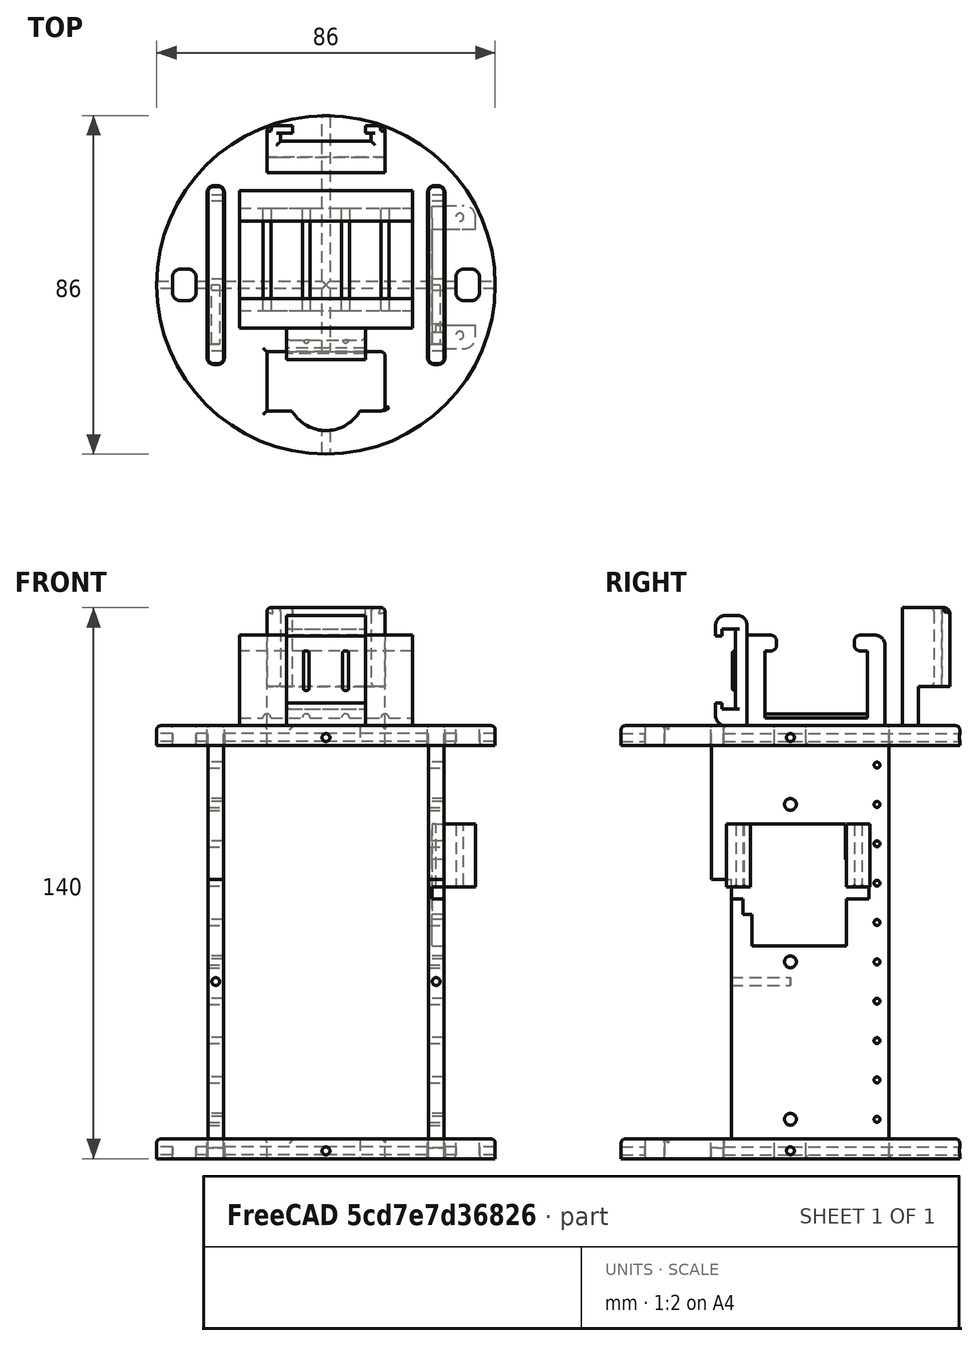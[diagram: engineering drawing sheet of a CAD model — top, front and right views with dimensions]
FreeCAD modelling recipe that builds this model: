
FCSTD DOCUMENT  (FreeCAD 1.0R39109 (Git))
Label: LateralDerecho_Capsula
License: All rights reserved
LicenseURL: http://en.wikipedia.org/wiki/All_rights_reserved
objects: Part::Cut×130, Part::Cylinder×98, Part::Fillet×96, Part::Box×72, Part::MultiFuse×37, Part::Offset×12, Part::Chamfer×1
note: 446 computed .brp shape members not serialized (recipe doc carries the construction recipe); baked Part::Feature solids carry a one-line shape summary decoded from their .brp

FEATURE [Part::Box] Box  label="Extensor"
  AttacherType = Attacher::AttachEngine3D
  Height = 66
  Length = 11
  Placement = pos=(30,-28,3) rot=(0,0,1;1.5708rad)
  Width = 60
FEATURE [Part::Box] Box001  label="Cubo001"
  AttacherType = Attacher::AttachEngine3D
  Height = 110
  Length = 45
  Placement = pos=(-30,25,0) rot=(0,0,-1;1.5708rad)
  Width = 4
FEATURE [Part::Box] Box002  label="Cubo002"
  AttacherType = Attacher::AttachEngine3D
  Height = 110
  Length = 45
  Placement = pos=(-30,25,0) rot=(0,0,-1;1.5708rad)
  Width = 4
FEATURE [Part::Box] Box003  label="Cubo003"
  AttacherType = Attacher::AttachEngine3D
  Height = 10
  Length = 30
  Placement = pos=(-15,-32,0) rot=(0,0,1;0rad)
  Width = 15
FEATURE [Part::Box] Box005  label="Cubo004"
  AttacherType = Attacher::AttachEngine3D
  Height = 15
  Length = 26
  Placement = pos=(-13,-23,110) rot=(0,0,1;0rad)
  Width = 35
FEATURE [Part::Box] Box006  label="Cubo005"
  AttacherType = Attacher::AttachEngine3D
  Height = 150
  Length = 6
  Width = 8
FEATURE [Part::Box] Box007  label="Cubo006"
  AttacherType = Attacher::AttachEngine3D
  Height = 150
  Length = 6
  Width = 8
FEATURE [Part::Box] Box008  label="Cubo007"
  AttacherType = Attacher::AttachEngine3D
  Height = 150
  Length = 6
  Width = 8
FEATURE [Part::Box] Box009  label="Cubo008"
  AttacherType = Attacher::AttachEngine3D
  Height = 150
  Length = 6
  Width = 8
FEATURE [Part::Box] Box010  label="Cubo009"
  AttacherType = Attacher::AttachEngine3D
  Height = 11.6
  Length = 20.8
  Placement = pos=(-10.5,-23,110) rot=(0,0,1;0rad)
  Width = 35
FEATURE [Part::Box] Box011  label="Cubo010"
  AttacherType = Attacher::AttachEngine3D
  Height = 11.6
  Length = 16
  Placement = pos=(-8,-23,116) rot=(0,0,1;0rad)
  Width = 35
FEATURE [Part::Box] Box095  label="Cubo095"
  AttacherType = Attacher::AttachEngine3D
  Height = 110
  Length = 45
  Placement = pos=(-30,25,0) rot=(0,0,-1;1.5708rad)
  Width = 4
FEATURE [Part::Box] Box096  label="Cubo096"
  AttacherType = Attacher::AttachEngine3D
  Height = 110
  Length = 45
  Placement = pos=(-30,25,0) rot=(0,0,-1;1.5708rad)
  Width = 4
FEATURE [Part::Box] Box097  label="Cubo097"
  AttacherType = Attacher::AttachEngine3D
  Height = 23
  Length = 24
  Width = 14
FEATURE [Part::Box] Box098  label="Cubo098"
  AttacherType = Attacher::AttachEngine3D
  Height = 3
  Length = 33.5
  Placement = pos=(-5,0,16) rot=(0,0,1;0rad)
  Width = 14
FEATURE [Part::Box] Box099  label="Cubo099"
  AttacherType = Attacher::AttachEngine3D
  Height = 1.4
  Length = 13
  Placement = pos=(9.8,5,28.6) rot=(0,0,1;0rad)
  Width = 4
FEATURE [Part::Box] Box100  label="Cubo100"
  AttacherType = Attacher::AttachEngine3D
  Height = 16
  Length = 10
  Placement = pos=(28,12.2,69) rot=(0,0,1;0rad)
  Width = 6
FEATURE [Part::Box] Box101  label="Cubo101"
  AttacherType = Attacher::AttachEngine3D
  Height = 16
  Length = 10
  Placement = pos=(28,-18.2,69) rot=(0,0,1;0rad)
  Width = 6
FEATURE [Part::Box] Box102  label="Extensor001"
  AttacherType = Attacher::AttachEngine3D
  Height = 66
  Length = 11
  Placement = pos=(30,-28,3) rot=(0,0,1;1.5708rad)
  Width = 60
FEATURE [Part::Box] Box104  label="Cubo102"
  AttacherType = Attacher::AttachEngine3D
  Height = 8
  Length = 20
  Width = 28
FEATURE [Part::Box] Box105  label="Cubo103"
  AttacherType = Attacher::AttachEngine3D
  Height = 2
  Length = 20.5
  Placement = pos=(0,4,4) rot=(0,0,1;0rad)
  Width = 20.5
FEATURE [Part::Box] Box106  label="Cubo104"
  AttacherType = Attacher::AttachEngine3D
  Height = 4
  Length = 20.5
  Placement = pos=(0,5,5) rot=(0,0,1;0rad)
  Width = 18.5
FEATURE [Part::Box] Box107  label="Cubo105"
  AttacherType = Attacher::AttachEngine3D
  Height = 8
  Length = 20
  Width = 30
FEATURE [Part::Box] Box108  label="Cubo106"
  AttacherType = Attacher::AttachEngine3D
  Height = 2
  Length = 20.5
  Placement = pos=(0,3.5,4) rot=(0,0,1;0rad)
  Width = 23
FEATURE [Part::Box] Box109  label="Cubo107"
  AttacherType = Attacher::AttachEngine3D
  Height = 4
  Length = 20.5
  Placement = pos=(0,5,5) rot=(0,0,1;0rad)
  Width = 18.5
FEATURE [Part::Box] Box110  label="Cubo108"
  AttacherType = Attacher::AttachEngine3D
  Height = 10
  Length = 20
  Placement = pos=(-9,-38,105) rot=(0,0,1;0rad)
  Width = 15
FEATURE [Part::Box] Box111  label="Cubo109"
  AttacherType = Attacher::AttachEngine3D
  Height = 110
  Length = 45
  Placement = pos=(-30,25,0) rot=(0,0,-1;1.5708rad)
  Width = 4
FEATURE [Part::Box] Box112  label="Extensor003"
  AttacherType = Attacher::AttachEngine3D
  Height = 66
  Length = 11
  Placement = pos=(30,-28,3) rot=(0,0,1;1.5708rad)
  Width = 60
FEATURE [Part::Box] Box113  label="Extensor004"
  AttacherType = Attacher::AttachEngine3D
  Height = 66
  Length = 11
  Placement = pos=(30,-28,3) rot=(0,0,1;1.5708rad)
  Width = 60
FEATURE [Part::Box] Box114  label="Cubo110"
  AttacherType = Attacher::AttachEngine3D
  Height = 110
  Length = 45
  Placement = pos=(-30,25,0) rot=(0,0,-1;1.5708rad)
  Width = 4
FEATURE [Part::Box] Box115  label="Cubo111"
  AttacherType = Attacher::AttachEngine3D
  Height = 23
  Length = 24
  Width = 14
FEATURE [Part::Box] Box116  label="Cubo112"
  AttacherType = Attacher::AttachEngine3D
  Height = 3
  Length = 33.5
  Placement = pos=(-5,0,16) rot=(0,0,1;0rad)
  Width = 14
FEATURE [Part::Box] Box117  label="Cubo113"
  AttacherType = Attacher::AttachEngine3D
  Height = 1.4
  Length = 13
  Placement = pos=(9.8,5,28.6) rot=(0,0,1;0rad)
  Width = 4
FEATURE [Part::Box] Box118  label="Cubo114"
  AttacherType = Attacher::AttachEngine3D
  Height = 16
  Length = 10
  Placement = pos=(28,12.2,69) rot=(0,0,1;0rad)
  Width = 6
FEATURE [Part::Box] Box119  label="Cubo115"
  AttacherType = Attacher::AttachEngine3D
  Height = 16
  Length = 10
  Placement = pos=(28,-18.2,69) rot=(0,0,1;0rad)
  Width = 6
FEATURE [Part::Box] Box120  label="Cubo116"
  AttacherType = Attacher::AttachEngine3D
  Height = 10
  Length = 4
  Placement = pos=(-30,-20,0) rot=(0,0,1;0rad)
  Width = 45
FEATURE [Part::Box] Box121  label="Cubo117"
  AttacherType = Attacher::AttachEngine3D
  Height = 10
  Length = 4
  Placement = pos=(-30,-20,0) rot=(0,0,1;0rad)
  Width = 45
FEATURE [Part::Box] Box122  label="Cubo118"
  AttacherType = Attacher::AttachEngine3D
  Height = 8
  Length = 20
  Width = 30
FEATURE [Part::Box] Box123  label="Cubo119"
  AttacherType = Attacher::AttachEngine3D
  Height = 2
  Length = 20.5
  Placement = pos=(0,3.5,4) rot=(0,0,1;0rad)
  Width = 23
FEATURE [Part::Box] Box124  label="Cubo120"
  AttacherType = Attacher::AttachEngine3D
  Height = 4
  Length = 20.5
  Placement = pos=(0,5,5) rot=(0,0,1;0rad)
  Width = 18.5
FEATURE [Part::Box] Box128  label="Cubo124"
  AttacherType = Attacher::AttachEngine3D
  Height = 30
  Length = 33
  Placement = pos=(-16,-43,115) rot=(0,0,1;0rad)
  Width = 30
FEATURE [Part::Box] Box129  label="Cubo125"
  AttacherType = Attacher::AttachEngine3D
  Height = 30
  Length = 33
  Placement = pos=(-16,13,110) rot=(0,0,1;0rad)
  Width = 30
FEATURE [Part::Box] Box130  label="Cubo126"
  AttacherType = Attacher::AttachEngine3D
  Height = 30
  Length = 30
  Placement = pos=(-16,13,110) rot=(0,0,1;0rad)
  Width = 4
FEATURE [Part::Box] Box131  label="Cubo127"
  AttacherType = Attacher::AttachEngine3D
  Height = 3.4
  Length = 21
  Placement = pos=(0,4.2,3) rot=(0,0,1;0rad)
  Width = 20.4
FEATURE [Part::Box] Box132  label="Cubo128"
  AttacherType = Attacher::AttachEngine3D
  Height = 4
  Length = 21
  Placement = pos=(0,5.75,6) rot=(0,0,1;0rad)
  Width = 17
FEATURE [Part::Box] Box133  label="Cubo129"
  AttacherType = Attacher::AttachEngine3D
  Height = 8
  Length = 20
  Width = 28
FEATURE [Part::Box] Box134  label="Cubo130"
  AttacherType = Attacher::AttachEngine3D
  Height = 16
  Length = 37
  Placement = pos=(-19,-15,110) rot=(0,0,1;0rad)
  Width = 30
FEATURE [Part::Box] Box135  label="Pila_ext"
  AttacherType = Attacher::AttachEngine3D
  Height = 25
  Length = 44
  Placement = pos=(-22,-11,110) rot=(0,0,1;0rad)
  Width = 35
FEATURE [Part::Box] Box136  label="Pila_int"
  AttacherType = Attacher::AttachEngine3D
  Height = 17
  Length = 44
  Placement = pos=(-22,-6.5,114) rot=(0,0,1;0rad)
  Width = 26
FEATURE [Part::Box] Box137  label="hueco_pila"
  AttacherType = Attacher::AttachEngine3D
  Height = 16.65
  Length = 44
  Placement = pos=(-22,-3.5,122) rot=(0,0,1;0rad)
  Width = 19.72
FEATURE [Part::Box] Box165  label="Cubo155"
  AttacherType = Attacher::AttachEngine3D
  Height = 17
  Length = 19
  Placement = pos=(27,-9.8,59) rot=(0,0,1;0rad)
  Width = 24
FEATURE [Part::Box] Box166  label="Cubo156"
  AttacherType = Attacher::AttachEngine3D
  Height = 66
  Length = 60
  Placement = pos=(-30,-20,5) rot=(0,0,1;0rad)
  Width = 5
FEATURE [Part::Box] Box167  label="Cubo157"
  AttacherType = Attacher::AttachEngine3D
  Height = 66
  Length = 60
  Placement = pos=(-30,-20,5) rot=(0,0,1;0rad)
  Width = 5
FEATURE [Part::Box] Box168  label="Cubo158"
  AttacherType = Attacher::AttachEngine3D
  Height = 3
  Length = 4
  Placement = pos=(27,7,66) rot=(0,0,1;0rad)
  Width = 13
FEATURE [Part::Box] Box169  label="Cubo159"
  AttacherType = Attacher::AttachEngine3D
  Height = 3
  Length = 4
  Placement = pos=(27,-9.8,56) rot=(0,0,1;0rad)
  Width = 24
FEATURE [Part::Box] Box170  label="Cubo160"
  AttacherType = Attacher::AttachEngine3D
  Height = 10
  Length = 30
  Placement = pos=(-15,-32,0) rot=(0,0,1;0rad)
  Width = 15
FEATURE [Part::Box] Box171  label="Cubo161"
  AttacherType = Attacher::AttachEngine3D
  Height = 150
  Length = 6
  Width = 8
FEATURE [Part::Box] Box172  label="Cubo162"
  AttacherType = Attacher::AttachEngine3D
  Height = 150
  Length = 6
  Width = 8
FEATURE [Part::Box] Box173  label="Cubo163"
  AttacherType = Attacher::AttachEngine3D
  Height = 110
  Length = 45
  Placement = pos=(-30,25,0) rot=(0,0,-1;1.5708rad)
  Width = 4
FEATURE [Part::Box] Box174  label="Extensor005"
  AttacherType = Attacher::AttachEngine3D
  Height = 66
  Length = 11
  Placement = pos=(30,-28,3) rot=(0,0,1;1.5708rad)
  Width = 60
FEATURE [Part::Box] Box175  label="Extensor006"
  AttacherType = Attacher::AttachEngine3D
  Height = 66
  Length = 11
  Placement = pos=(30,-28,3) rot=(0,0,1;1.5708rad)
  Width = 60
FEATURE [Part::Box] Box176  label="Cubo164"
  AttacherType = Attacher::AttachEngine3D
  Height = 110
  Length = 45
  Placement = pos=(-30,25,0) rot=(0,0,-1;1.5708rad)
  Width = 4
FEATURE [Part::Box] Box177  label="Cubo165"
  AttacherType = Attacher::AttachEngine3D
  Height = 23
  Length = 24
  Width = 14
FEATURE [Part::Box] Box178  label="Cubo166"
  AttacherType = Attacher::AttachEngine3D
  Height = 3
  Length = 33.5
  Placement = pos=(-5,0,16) rot=(0,0,1;0rad)
  Width = 14
FEATURE [Part::Box] Box179  label="Cubo167"
  AttacherType = Attacher::AttachEngine3D
  Height = 1.4
  Length = 13
  Placement = pos=(9.8,5,28.6) rot=(0,0,1;0rad)
  Width = 4
FEATURE [Part::Box] Box180  label="Cubo168"
  AttacherType = Attacher::AttachEngine3D
  Height = 16
  Length = 10
  Placement = pos=(28,12.2,69) rot=(0,0,1;0rad)
  Width = 6
FEATURE [Part::Box] Box181  label="Cubo169"
  AttacherType = Attacher::AttachEngine3D
  Height = 16
  Length = 10
  Placement = pos=(28,-18.2,69) rot=(0,0,1;0rad)
  Width = 6
FEATURE [Part::Box] Box182  label="Cubo170"
  AttacherType = Attacher::AttachEngine3D
  Height = 10
  Length = 4
  Placement = pos=(-30,-20,0) rot=(0,0,1;0rad)
  Width = 45
FEATURE [Part::Box] Box183  label="Cubo171"
  AttacherType = Attacher::AttachEngine3D
  Height = 10
  Length = 4
  Placement = pos=(-30,-20,0) rot=(0,0,1;0rad)
  Width = 45
FEATURE [Part::Box] Box184  label="Cubo172"
  AttacherType = Attacher::AttachEngine3D
  Height = 10
  Length = 120
  Placement = pos=(-50,-47,100) rot=(0,0,1;0rad)
  Width = 120
FEATURE [Part::Box] Box197  label="Cubo184"
  AttacherType = Attacher::AttachEngine3D
  Height = 16
  Length = 3
  Placement = pos=(27,12,69) rot=(0,0,1;0rad)
  Width = 2
FEATURE [Part::Box] Box198  label="Cubo185"
  AttacherType = Attacher::AttachEngine3D
  Height = 24
  Length = 3
  Placement = pos=(27,14.2,54) rot=(1,0,0;1.5708rad)
  Width = 4
FEATURE [Part::Cut] Cut016
  Base = -> Box005
  Tool = -> Box010
FEATURE [Part::Cut] Cut017
  Base = -> Cut016
  Placement = pos=(-5,0,0) rot=(0,0,1;1.5708rad)
  Tool = -> Box011
FEATURE [Part::Cut] Cut115
  Base = -> Box104
  Tool = -> Box105
FEATURE [Part::Cut] Cut116
  Base = -> Cut115
  Tool = -> Box106
FEATURE [Part::Cut] Cut117
  Base = -> Box107
  Tool = -> Box108
FEATURE [Part::Cut] Cut118
  Base = -> Cut117
  Tool = -> Box109
FEATURE [Part::Cut] Cut143
  Base = -> Box122
  Tool = -> Box123
FEATURE [Part::Cut] Cut144
  Base = -> Cut143
  Tool = -> Box124
FEATURE [Part::Cut] Cut149
  Base = -> Box133
  Tool = -> Box131
FEATURE [Part::Cut] Cut150
  Base = -> Cut149
  Tool = -> Box132
FEATURE [Part::Cut] Cut152
  Base = -> Box135
  Tool = -> Box136
FEATURE [Part::Cut] Cut153  label="PortaPIlas_9V"
  Base = -> Cut152
  Placement = pos=(0,0,-2) rot=(0,0,1;0rad)
  Tool = -> Box137
FEATURE [Part::Cylinder] Cylinder  label="Cilindro"
  Angle = 360
  AttacherType = Attacher::AttachEngine3D
  FirstAngle = 0
  Height = 5
  Radius = 43
  SecondAngle = 0
FEATURE [Part::Cylinder] Cylinder002  label="Cilindro002"
  Angle = 360
  AttacherType = Attacher::AttachEngine3D
  FirstAngle = 0
  Height = 20
  Placement = pos=(0,44,1.5) rot=(1,0,0;1.5708rad)
  Radius = 0.5
  SecondAngle = 0
FEATURE [Part::Cylinder] Cylinder003  label="Cilindro003"
  Angle = 360
  AttacherType = Attacher::AttachEngine3D
  FirstAngle = 0
  Height = 20
  Placement = pos=(0,-26,1.5) rot=(1,0,0;1.5708rad)
  Radius = 0.5
  SecondAngle = 0
FEATURE [Part::Cylinder] Cylinder004  label="Cilindro004"
  Angle = 360
  AttacherType = Attacher::AttachEngine3D
  FirstAngle = 0
  Height = 3
  Radius = 43
  SecondAngle = 0
FEATURE [Part::Cylinder] Cylinder005  label="Cilindro005"
  Angle = 360
  AttacherType = Attacher::AttachEngine3D
  FirstAngle = 0
  Height = 20
  Placement = pos=(0,44,1.5) rot=(1,0,0;1.5708rad)
  Radius = 0.5
  SecondAngle = 0
FEATURE [Part::Cylinder] Cylinder006  label="Cilindro006"
  Angle = 360
  AttacherType = Attacher::AttachEngine3D
  FirstAngle = 0
  Height = 20
  Placement = pos=(0,-26,1.5) rot=(1,0,0;1.5708rad)
  Radius = 0.5
  SecondAngle = 0
FEATURE [Part::Cylinder] Cylinder008  label="Cilindro008"
  Angle = 360
  AttacherType = Attacher::AttachEngine3D
  FirstAngle = 0
  Height = 100
  Placement = pos=(-46,0,50) rot=(0,1,0;1.5708rad)
  Radius = 1.5
  SecondAngle = 0
FEATURE [Part::Cylinder] Cylinder009  label="Cilindro009"
  Angle = 360
  AttacherType = Attacher::AttachEngine3D
  FirstAngle = 0
  Height = 100
  Placement = pos=(-46,0,90) rot=(0,1,0;1.5708rad)
  Radius = 1.5
  SecondAngle = 0
FEATURE [Part::Cylinder] Cylinder010  label="Cilindro010"
  Angle = 360
  AttacherType = Attacher::AttachEngine3D
  FirstAngle = 0
  Height = 100
  Placement = pos=(-46,0,10) rot=(0,1,0;1.5708rad)
  Radius = 1.5
  SecondAngle = 0
FEATURE [Part::Cylinder] Cylinder011  label="Cilindro011"
  Angle = 360
  AttacherType = Attacher::AttachEngine3D
  FirstAngle = 0
  Height = 10
  Placement = pos=(0,-27,0) rot=(0,0,1;0rad)
  Radius = 10
  SecondAngle = 0
FEATURE [Part::Cylinder] Cylinder071  label="Cilindro071"
  Angle = 360
  AttacherType = Attacher::AttachEngine3D
  FirstAngle = 0
  Height = 100
  Placement = pos=(-46,0,50) rot=(0,1,0;1.5708rad)
  Radius = 1.5
  SecondAngle = 0
FEATURE [Part::Cylinder] Cylinder072  label="Cilindro072"
  Angle = 360
  AttacherType = Attacher::AttachEngine3D
  FirstAngle = 0
  Height = 100
  Placement = pos=(-46,0,90) rot=(0,1,0;1.5708rad)
  Radius = 1.5
  SecondAngle = 0
FEATURE [Part::Cylinder] Cylinder073  label="Cilindro073"
  Angle = 360
  AttacherType = Attacher::AttachEngine3D
  FirstAngle = 0
  Height = 100
  Placement = pos=(-46,0,10) rot=(0,1,0;1.5708rad)
  Radius = 1.5
  SecondAngle = 0
FEATURE [Part::Cylinder] Cylinder074  label="Cilindro074"
  Angle = 360
  AttacherType = Attacher::AttachEngine3D
  FirstAngle = 0
  Height = 3
  Placement = pos=(7,7,23) rot=(0,0,1;0rad)
  Radius = 7
  SecondAngle = 0
FEATURE [Part::Cylinder] Cylinder075  label="Cilindro075"
  Angle = 360
  AttacherType = Attacher::AttachEngine3D
  FirstAngle = 0
  Height = 3
  Placement = pos=(14,7,23) rot=(0,0,1;0rad)
  Radius = 2
  SecondAngle = 0
FEATURE [Part::Cylinder] Cylinder076  label="Cilindro076"
  Angle = 360
  AttacherType = Attacher::AttachEngine3D
  FirstAngle = 0
  Height = 10
  Placement = pos=(-3.2,7,12) rot=(0,0,1;0rad)
  Radius = 1.65
  SecondAngle = 0
FEATURE [Part::Cylinder] Cylinder077  label="Cilindro077"
  Angle = 360
  AttacherType = Attacher::AttachEngine3D
  FirstAngle = 0
  Height = 10
  Placement = pos=(26.8,7,12) rot=(0,0,1;0rad)
  Radius = 1.65
  SecondAngle = 0
FEATURE [Part::Cylinder] Cylinder078  label="Cilindro078"
  Angle = 360
  AttacherType = Attacher::AttachEngine3D
  FirstAngle = 0
  Height = 4
  Placement = pos=(7,7,26) rot=(0,0,1;0rad)
  Radius = 3.5
  SecondAngle = 0
FEATURE [Part::Cylinder] Cylinder079  label="Cilindro079"
  Angle = 360
  AttacherType = Attacher::AttachEngine3D
  FirstAngle = 0
  Height = 10
  Placement = pos=(21,7,25) rot=(0,0,1;0rad)
  Radius = 0.25
  SecondAngle = 0
FEATURE [Part::Cylinder] Cylinder080  label="Cilindro080"
  Angle = 360
  AttacherType = Attacher::AttachEngine3D
  FirstAngle = 0
  Height = 10
  Placement = pos=(19,7,25) rot=(0,0,1;0rad)
  Radius = 0.25
  SecondAngle = 0
FEATURE [Part::Cylinder] Cylinder081  label="Cilindro081"
  Angle = 360
  AttacherType = Attacher::AttachEngine3D
  FirstAngle = 0
  Height = 10
  Placement = pos=(17,7,25) rot=(0,0,1;0rad)
  Radius = 0.25
  SecondAngle = 0
FEATURE [Part::Cylinder] Cylinder082  label="Cilindro082"
  Angle = 360
  AttacherType = Attacher::AttachEngine3D
  FirstAngle = 0
  Height = 10
  Placement = pos=(15,7,27) rot=(0,0,1;0rad)
  Radius = 0.25
  SecondAngle = 0
FEATURE [Part::Cylinder] Cylinder083  label="Cilindro083"
  Angle = 360
  AttacherType = Attacher::AttachEngine3D
  FirstAngle = 0
  Height = 10
  Placement = pos=(13,7,27) rot=(0,0,1;0rad)
  Radius = 0.25
  SecondAngle = 0
FEATURE [Part::Cylinder] Cylinder084  label="Cilindro084"
  Angle = 360
  AttacherType = Attacher::AttachEngine3D
  FirstAngle = 0
  Height = 20
  Placement = pos=(34,-14.8,66) rot=(0,0,1;0rad)
  Radius = 1
  SecondAngle = 0
FEATURE [Part::Cylinder] Cylinder085  label="Cilindro085"
  Angle = 360
  AttacherType = Attacher::AttachEngine3D
  FirstAngle = 0
  Height = 20
  Placement = pos=(34,15.2,66) rot=(0,0,1;0rad)
  Radius = 1
  SecondAngle = 0
FEATURE [Part::Cylinder] Cylinder086  label="Cilindro086"
  Angle = 360
  AttacherType = Attacher::AttachEngine3D
  FirstAngle = 0
  Height = 100
  Placement = pos=(-46,0,50) rot=(0,1,0;1.5708rad)
  Radius = 1.5
  SecondAngle = 0
FEATURE [Part::Cylinder] Cylinder087  label="Cilindro087"
  Angle = 360
  AttacherType = Attacher::AttachEngine3D
  FirstAngle = 0
  Height = 100
  Placement = pos=(-46,0,90) rot=(0,1,0;1.5708rad)
  Radius = 1.5
  SecondAngle = 0
FEATURE [Part::Cylinder] Cylinder088  label="Cilindro088"
  Angle = 360
  AttacherType = Attacher::AttachEngine3D
  FirstAngle = 0
  Height = 100
  Placement = pos=(-46,0,10) rot=(0,1,0;1.5708rad)
  Radius = 1.5
  SecondAngle = 0
FEATURE [Part::Cylinder] Cylinder089  label="Cilindro089"
  Angle = 360
  AttacherType = Attacher::AttachEngine3D
  FirstAngle = 0
  Height = 100
  Placement = pos=(-46,0,50) rot=(0,1,0;1.5708rad)
  Radius = 1.5
  SecondAngle = 0
FEATURE [Part::Cylinder] Cylinder090  label="Cilindro090"
  Angle = 360
  AttacherType = Attacher::AttachEngine3D
  FirstAngle = 0
  Height = 100
  Placement = pos=(-46,0,90) rot=(0,1,0;1.5708rad)
  Radius = 1.5
  SecondAngle = 0
FEATURE [Part::Cylinder] Cylinder091  label="Cilindro091"
  Angle = 360
  AttacherType = Attacher::AttachEngine3D
  FirstAngle = 0
  Height = 100
  Placement = pos=(-46,0,10) rot=(0,1,0;1.5708rad)
  Radius = 1.5
  SecondAngle = 0
FEATURE [Part::Cylinder] Cylinder092  label="Cilindro092"
  Angle = 360
  AttacherType = Attacher::AttachEngine3D
  FirstAngle = 0
  Height = 3
  Placement = pos=(7,7,23) rot=(0,0,1;0rad)
  Radius = 7
  SecondAngle = 0
FEATURE [Part::Cylinder] Cylinder093  label="Cilindro093"
  Angle = 360
  AttacherType = Attacher::AttachEngine3D
  FirstAngle = 0
  Height = 3
  Placement = pos=(14,7,23) rot=(0,0,1;0rad)
  Radius = 2
  SecondAngle = 0
FEATURE [Part::Cylinder] Cylinder094  label="Cilindro094"
  Angle = 360
  AttacherType = Attacher::AttachEngine3D
  FirstAngle = 0
  Height = 10
  Placement = pos=(-3.2,7,12) rot=(0,0,1;0rad)
  Radius = 1.65
  SecondAngle = 0
FEATURE [Part::Cylinder] Cylinder095  label="Cilindro095"
  Angle = 360
  AttacherType = Attacher::AttachEngine3D
  FirstAngle = 0
  Height = 10
  Placement = pos=(26.8,7,12) rot=(0,0,1;0rad)
  Radius = 1.65
  SecondAngle = 0
FEATURE [Part::Cylinder] Cylinder096  label="Cilindro096"
  Angle = 360
  AttacherType = Attacher::AttachEngine3D
  FirstAngle = 0
  Height = 4
  Placement = pos=(7,7,26) rot=(0,0,1;0rad)
  Radius = 3.5
  SecondAngle = 0
FEATURE [Part::Cylinder] Cylinder097  label="Cilindro097"
  Angle = 360
  AttacherType = Attacher::AttachEngine3D
  FirstAngle = 0
  Height = 10
  Placement = pos=(21,7,25) rot=(0,0,1;0rad)
  Radius = 0.25
  SecondAngle = 0
FEATURE [Part::Cylinder] Cylinder098  label="Cilindro098"
  Angle = 360
  AttacherType = Attacher::AttachEngine3D
  FirstAngle = 0
  Height = 10
  Placement = pos=(19,7,25) rot=(0,0,1;0rad)
  Radius = 0.25
  SecondAngle = 0
FEATURE [Part::Cylinder] Cylinder099  label="Cilindro099"
  Angle = 360
  AttacherType = Attacher::AttachEngine3D
  FirstAngle = 0
  Height = 10
  Placement = pos=(17,7,25) rot=(0,0,1;0rad)
  Radius = 0.25
  SecondAngle = 0
FEATURE [Part::Cylinder] Cylinder100  label="Cilindro100"
  Angle = 360
  AttacherType = Attacher::AttachEngine3D
  FirstAngle = 0
  Height = 10
  Placement = pos=(15,7,27) rot=(0,0,1;0rad)
  Radius = 0.25
  SecondAngle = 0
FEATURE [Part::Cylinder] Cylinder101  label="Cilindro101"
  Angle = 360
  AttacherType = Attacher::AttachEngine3D
  FirstAngle = 0
  Height = 10
  Placement = pos=(13,7,27) rot=(0,0,1;0rad)
  Radius = 0.25
  SecondAngle = 0
FEATURE [Part::Cylinder] Cylinder102  label="Cilindro102"
  Angle = 360
  AttacherType = Attacher::AttachEngine3D
  FirstAngle = 0
  Height = 20
  Placement = pos=(34,-14.8,66) rot=(0,0,1;0rad)
  Radius = 1
  SecondAngle = 0
FEATURE [Part::Cylinder] Cylinder103  label="Cilindro103"
  Angle = 360
  AttacherType = Attacher::AttachEngine3D
  FirstAngle = 0
  Height = 20
  Placement = pos=(34,15.2,66) rot=(0,0,1;0rad)
  Radius = 1
  SecondAngle = 0
FEATURE [Part::Cylinder] Cylinder104  label="Cilindro104"
  Angle = 360
  AttacherType = Attacher::AttachEngine3D
  FirstAngle = 0
  Height = 100
  Placement = pos=(0,52,2) rot=(1,0,0;1.5708rad)
  Radius = 1
  SecondAngle = 0
FEATURE [Part::Cylinder] Cylinder109  label="Cilindro109"
  Angle = 360
  AttacherType = Attacher::AttachEngine3D
  FirstAngle = 0
  Height = 15
  Placement = pos=(-28,0,45) rot=(1,0,0;1.5708rad)
  Radius = 1
  SecondAngle = 0
FEATURE [Part::Cylinder] Cylinder110  label="Cilindro110"
  Angle = 360
  AttacherType = Attacher::AttachEngine3D
  FirstAngle = 0
  Height = 15
  Placement = pos=(28,0,45) rot=(1,0,0;1.5708rad)
  Radius = 1
  SecondAngle = 0
FEATURE [Part::Cylinder] Cylinder111  label="Cilindro111"
  Angle = 360
  AttacherType = Attacher::AttachEngine3D
  FirstAngle = 0
  Height = 67
  Placement = pos=(-33,22,10) rot=(0,1,0;1.5708rad)
  Radius = 0.75
  SecondAngle = 0
FEATURE [Part::Cylinder] Cylinder112  label="Cilindro112"
  Angle = 360
  AttacherType = Attacher::AttachEngine3D
  FirstAngle = 0
  Height = 67
  Placement = pos=(-33,22,100) rot=(0,1,0;1.5708rad)
  Radius = 0.75
  SecondAngle = 0
FEATURE [Part::Cylinder] Cylinder113  label="Cilindro113"
  Angle = 360
  AttacherType = Attacher::AttachEngine3D
  FirstAngle = 0
  Height = 67
  Placement = pos=(-33,22,20) rot=(0,1,0;1.5708rad)
  Radius = 0.75
  SecondAngle = 0
FEATURE [Part::Cylinder] Cylinder114  label="Cilindro114"
  Angle = 360
  AttacherType = Attacher::AttachEngine3D
  FirstAngle = 0
  Height = 67
  Placement = pos=(-33,22,30) rot=(0,1,0;1.5708rad)
  Radius = 0.75
  SecondAngle = 0
FEATURE [Part::Cylinder] Cylinder115  label="Cilindro115"
  Angle = 360
  AttacherType = Attacher::AttachEngine3D
  FirstAngle = 0
  Height = 67
  Placement = pos=(-33,22,40) rot=(0,1,0;1.5708rad)
  Radius = 0.75
  SecondAngle = 0
FEATURE [Part::Cylinder] Cylinder116  label="Cilindro116"
  Angle = 360
  AttacherType = Attacher::AttachEngine3D
  FirstAngle = 0
  Height = 67
  Placement = pos=(-33,22,50) rot=(0,1,0;1.5708rad)
  Radius = 0.75
  SecondAngle = 0
FEATURE [Part::Cylinder] Cylinder117  label="Cilindro117"
  Angle = 360
  AttacherType = Attacher::AttachEngine3D
  FirstAngle = 0
  Height = 67
  Placement = pos=(-33,22,60) rot=(0,1,0;1.5708rad)
  Radius = 0.75
  SecondAngle = 0
FEATURE [Part::Cylinder] Cylinder118  label="Cilindro118"
  Angle = 360
  AttacherType = Attacher::AttachEngine3D
  FirstAngle = 0
  Height = 67
  Placement = pos=(-33,22,70) rot=(0,1,0;1.5708rad)
  Radius = 0.75
  SecondAngle = 0
FEATURE [Part::Cylinder] Cylinder119  label="Cilindro119"
  Angle = 360
  AttacherType = Attacher::AttachEngine3D
  FirstAngle = 0
  Height = 67
  Placement = pos=(-33,22,80) rot=(0,1,0;1.5708rad)
  Radius = 0.75
  SecondAngle = 0
FEATURE [Part::Cylinder] Cylinder120  label="Cilindro120"
  Angle = 360
  AttacherType = Attacher::AttachEngine3D
  FirstAngle = 0
  Height = 67
  Placement = pos=(-33,22,90) rot=(0,1,0;1.5708rad)
  Radius = 0.75
  SecondAngle = 0
FEATURE [Part::Cylinder] Cylinder121  label="Cilindro121"
  Angle = 360
  AttacherType = Attacher::AttachEngine3D
  FirstAngle = 0
  Height = 67
  Placement = pos=(-33,22,10) rot=(0,1,0;1.5708rad)
  Radius = 0.75
  SecondAngle = 0
FEATURE [Part::Cylinder] Cylinder122  label="Cilindro122"
  Angle = 360
  AttacherType = Attacher::AttachEngine3D
  FirstAngle = 0
  Height = 67
  Placement = pos=(-33,22,100) rot=(0,1,0;1.5708rad)
  Radius = 0.75
  SecondAngle = 0
FEATURE [Part::Cylinder] Cylinder123  label="Cilindro123"
  Angle = 360
  AttacherType = Attacher::AttachEngine3D
  FirstAngle = 0
  Height = 67
  Placement = pos=(-33,22,20) rot=(0,1,0;1.5708rad)
  Radius = 0.75
  SecondAngle = 0
FEATURE [Part::Cylinder] Cylinder124  label="Cilindro124"
  Angle = 360
  AttacherType = Attacher::AttachEngine3D
  FirstAngle = 0
  Height = 67
  Placement = pos=(-33,22,30) rot=(0,1,0;1.5708rad)
  Radius = 0.75
  SecondAngle = 0
FEATURE [Part::Cylinder] Cylinder125  label="Cilindro125"
  Angle = 360
  AttacherType = Attacher::AttachEngine3D
  FirstAngle = 0
  Height = 67
  Placement = pos=(-33,22,40) rot=(0,1,0;1.5708rad)
  Radius = 0.75
  SecondAngle = 0
FEATURE [Part::Cylinder] Cylinder126  label="Cilindro126"
  Angle = 360
  AttacherType = Attacher::AttachEngine3D
  FirstAngle = 0
  Height = 67
  Placement = pos=(-33,22,50) rot=(0,1,0;1.5708rad)
  Radius = 0.75
  SecondAngle = 0
FEATURE [Part::Cylinder] Cylinder127  label="Cilindro127"
  Angle = 360
  AttacherType = Attacher::AttachEngine3D
  FirstAngle = 0
  Height = 67
  Placement = pos=(-33,22,60) rot=(0,1,0;1.5708rad)
  Radius = 0.75
  SecondAngle = 0
FEATURE [Part::Cylinder] Cylinder128  label="Cilindro128"
  Angle = 360
  AttacherType = Attacher::AttachEngine3D
  FirstAngle = 0
  Height = 67
  Placement = pos=(-33,22,70) rot=(0,1,0;1.5708rad)
  Radius = 0.75
  SecondAngle = 0
FEATURE [Part::Cylinder] Cylinder129  label="Cilindro129"
  Angle = 360
  AttacherType = Attacher::AttachEngine3D
  FirstAngle = 0
  Height = 67
  Placement = pos=(-33,22,80) rot=(0,1,0;1.5708rad)
  Radius = 0.75
  SecondAngle = 0
FEATURE [Part::Cylinder] Cylinder130  label="Cilindro130"
  Angle = 360
  AttacherType = Attacher::AttachEngine3D
  FirstAngle = 0
  Height = 67
  Placement = pos=(-33,22,90) rot=(0,1,0;1.5708rad)
  Radius = 0.75
  SecondAngle = 0
FEATURE [Part::Cylinder] Cylinder131  label="Cilindro131"
  Angle = 360
  AttacherType = Attacher::AttachEngine3D
  FirstAngle = 0
  Height = 67
  Placement = pos=(-33,22,70) rot=(0,1,0;1.5708rad)
  Radius = 0.75
  SecondAngle = 0
FEATURE [Part::Cylinder] Cylinder133  label="Cilindro133"
  Angle = 360
  AttacherType = Attacher::AttachEngine3D
  FirstAngle = 0
  Height = 110
  Placement = pos=(-55,0,2) rot=(0.57735,0.57735,0.57735;2.0944rad)
  Radius = 1
  SecondAngle = 0
FEATURE [Part::Cylinder] Cylinder134  label="Cilindro134"
  Angle = 360
  AttacherType = Attacher::AttachEngine3D
  FirstAngle = 0
  Height = 5
  Radius = 43
  SecondAngle = 0
FEATURE [Part::Cylinder] Cylinder135  label="Cilindro135"
  Angle = 360
  AttacherType = Attacher::AttachEngine3D
  FirstAngle = 0
  Height = 20
  Placement = pos=(0,44,1.5) rot=(1,0,0;1.5708rad)
  Radius = 0.5
  SecondAngle = 0
FEATURE [Part::Cylinder] Cylinder136  label="Cilindro136"
  Angle = 360
  AttacherType = Attacher::AttachEngine3D
  FirstAngle = 0
  Height = 20
  Placement = pos=(0,-26,1.5) rot=(1,0,0;1.5708rad)
  Radius = 0.5
  SecondAngle = 0
FEATURE [Part::Cylinder] Cylinder137  label="Cilindro137"
  Angle = 360
  AttacherType = Attacher::AttachEngine3D
  FirstAngle = 0
  Height = 10
  Placement = pos=(0,-27,0) rot=(0,0,1;0rad)
  Radius = 10
  SecondAngle = 0
FEATURE [Part::Cylinder] Cylinder138  label="Cilindro138"
  Angle = 360
  AttacherType = Attacher::AttachEngine3D
  FirstAngle = 0
  Height = 100
  Placement = pos=(-46,0,50) rot=(0,1,0;1.5708rad)
  Radius = 1.5
  SecondAngle = 0
FEATURE [Part::Cylinder] Cylinder139  label="Cilindro139"
  Angle = 360
  AttacherType = Attacher::AttachEngine3D
  FirstAngle = 0
  Height = 100
  Placement = pos=(-46,0,90) rot=(0,1,0;1.5708rad)
  Radius = 1.5
  SecondAngle = 0
FEATURE [Part::Cylinder] Cylinder140  label="Cilindro140"
  Angle = 360
  AttacherType = Attacher::AttachEngine3D
  FirstAngle = 0
  Height = 100
  Placement = pos=(-46,0,10) rot=(0,1,0;1.5708rad)
  Radius = 1.5
  SecondAngle = 0
FEATURE [Part::Cylinder] Cylinder141  label="Cilindro141"
  Angle = 360
  AttacherType = Attacher::AttachEngine3D
  FirstAngle = 0
  Height = 100
  Placement = pos=(-46,0,50) rot=(0,1,0;1.5708rad)
  Radius = 1.5
  SecondAngle = 0
FEATURE [Part::Cylinder] Cylinder142  label="Cilindro142"
  Angle = 360
  AttacherType = Attacher::AttachEngine3D
  FirstAngle = 0
  Height = 100
  Placement = pos=(-46,0,90) rot=(0,1,0;1.5708rad)
  Radius = 1.5
  SecondAngle = 0
FEATURE [Part::Cylinder] Cylinder143  label="Cilindro143"
  Angle = 360
  AttacherType = Attacher::AttachEngine3D
  FirstAngle = 0
  Height = 100
  Placement = pos=(-46,0,10) rot=(0,1,0;1.5708rad)
  Radius = 1.5
  SecondAngle = 0
FEATURE [Part::Cylinder] Cylinder144  label="Cilindro144"
  Angle = 360
  AttacherType = Attacher::AttachEngine3D
  FirstAngle = 0
  Height = 3
  Placement = pos=(7,7,23) rot=(0,0,1;0rad)
  Radius = 7
  SecondAngle = 0
FEATURE [Part::Cylinder] Cylinder145  label="Cilindro145"
  Angle = 360
  AttacherType = Attacher::AttachEngine3D
  FirstAngle = 0
  Height = 3
  Placement = pos=(14,7,23) rot=(0,0,1;0rad)
  Radius = 2
  SecondAngle = 0
FEATURE [Part::Cylinder] Cylinder146  label="Cilindro146"
  Angle = 360
  AttacherType = Attacher::AttachEngine3D
  FirstAngle = 0
  Height = 10
  Placement = pos=(-3.2,7,12) rot=(0,0,1;0rad)
  Radius = 1.65
  SecondAngle = 0
FEATURE [Part::Cylinder] Cylinder147  label="Cilindro147"
  Angle = 360
  AttacherType = Attacher::AttachEngine3D
  FirstAngle = 0
  Height = 10
  Placement = pos=(26.8,7,12) rot=(0,0,1;0rad)
  Radius = 1.65
  SecondAngle = 0
FEATURE [Part::Cylinder] Cylinder148  label="Cilindro148"
  Angle = 360
  AttacherType = Attacher::AttachEngine3D
  FirstAngle = 0
  Height = 4
  Placement = pos=(7,7,26) rot=(0,0,1;0rad)
  Radius = 3.5
  SecondAngle = 0
FEATURE [Part::Cylinder] Cylinder149  label="Cilindro149"
  Angle = 360
  AttacherType = Attacher::AttachEngine3D
  FirstAngle = 0
  Height = 10
  Placement = pos=(21,7,25) rot=(0,0,1;0rad)
  Radius = 0.25
  SecondAngle = 0
FEATURE [Part::Cylinder] Cylinder150  label="Cilindro150"
  Angle = 360
  AttacherType = Attacher::AttachEngine3D
  FirstAngle = 0
  Height = 10
  Placement = pos=(19,7,25) rot=(0,0,1;0rad)
  Radius = 0.25
  SecondAngle = 0
FEATURE [Part::Cylinder] Cylinder151  label="Cilindro151"
  Angle = 360
  AttacherType = Attacher::AttachEngine3D
  FirstAngle = 0
  Height = 10
  Placement = pos=(17,7,25) rot=(0,0,1;0rad)
  Radius = 0.25
  SecondAngle = 0
FEATURE [Part::Cylinder] Cylinder152  label="Cilindro152"
  Angle = 360
  AttacherType = Attacher::AttachEngine3D
  FirstAngle = 0
  Height = 10
  Placement = pos=(15,7,27) rot=(0,0,1;0rad)
  Radius = 0.25
  SecondAngle = 0
FEATURE [Part::Cylinder] Cylinder153  label="Cilindro153"
  Angle = 360
  AttacherType = Attacher::AttachEngine3D
  FirstAngle = 0
  Height = 10
  Placement = pos=(13,7,27) rot=(0,0,1;0rad)
  Radius = 0.25
  SecondAngle = 0
FEATURE [Part::Cylinder] Cylinder154  label="Cilindro154"
  Angle = 360
  AttacherType = Attacher::AttachEngine3D
  FirstAngle = 0
  Height = 20
  Placement = pos=(34,-14.8,66) rot=(0,0,1;0rad)
  Radius = 1
  SecondAngle = 0
FEATURE [Part::Cylinder] Cylinder155  label="Cilindro155"
  Angle = 360
  AttacherType = Attacher::AttachEngine3D
  FirstAngle = 0
  Height = 20
  Placement = pos=(34,15.2,66) rot=(0,0,1;0rad)
  Radius = 1
  SecondAngle = 0
FEATURE [Part::Cylinder] Cylinder156  label="Cilindro156"
  Angle = 360
  AttacherType = Attacher::AttachEngine3D
  FirstAngle = 0
  Height = 100
  Placement = pos=(0,52,2) rot=(1,0,0;1.5708rad)
  Radius = 1
  SecondAngle = 0
FEATURE [Part::Cylinder] Cylinder157  label="Cilindro157"
  Angle = 360
  AttacherType = Attacher::AttachEngine3D
  FirstAngle = 0
  Height = 110
  Placement = pos=(-55,0,2) rot=(0.57735,0.57735,0.57735;2.0944rad)
  Radius = 1
  SecondAngle = 0
FEATURE [Part::Cylinder] Cylinder158  label="Cilindro158"
  Angle = 360
  AttacherType = Attacher::AttachEngine3D
  FirstAngle = 0
  Height = 29
  Placement = pos=(-15,22,112) rot=(1,0,0;1.5708rad)
  Radius = 1
  SecondAngle = 0
FEATURE [Part::Cylinder] Cylinder159  label="Cilindro159"
  Angle = 360
  AttacherType = Attacher::AttachEngine3D
  FirstAngle = 0
  Height = 29
  Placement = pos=(-5,22,112) rot=(1,0,0;1.5708rad)
  Radius = 1
  SecondAngle = 0
FEATURE [Part::Cylinder] Cylinder160  label="Cilindro160"
  Angle = 360
  AttacherType = Attacher::AttachEngine3D
  FirstAngle = 0
  Height = 29
  Placement = pos=(5,22,112) rot=(1,0,0;1.5708rad)
  Radius = 1
  SecondAngle = 0
FEATURE [Part::Cylinder] Cylinder161  label="Cilindro161"
  Angle = 360
  AttacherType = Attacher::AttachEngine3D
  FirstAngle = 0
  Height = 29
  Placement = pos=(15,22,112) rot=(1,0,0;1.5708rad)
  Radius = 1
  SecondAngle = 0
FEATURE [Part::Cylinder] Cylinder162  label="Cilindro162"
  Angle = 360
  AttacherType = Attacher::AttachEngine3D
  FirstAngle = 0
  Height = 10
  Placement = pos=(-5,-14,119) rot=(0,0,1;0rad)
  Radius = 0.75
  SecondAngle = 0
FEATURE [Part::Cylinder] Cylinder163  label="Cilindro163"
  Angle = 360
  AttacherType = Attacher::AttachEngine3D
  FirstAngle = 0
  Height = 10
  Placement = pos=(5,-14,119) rot=(0,0,1;0rad)
  Radius = 0.75
  SecondAngle = 0
FEATURE [Part::Fillet] Fillet
  Base = -> Cylinder
  EdgeLinks = -> Cylinder [Edge3]
  Edges = 1 edges r=1: [Edge3]
FEATURE [Part::Cut] Cut
  Base = -> Fillet
  Tool = -> Cylinder003
FEATURE [Part::Cut] Cut001  label="BaseInf"
  Base = -> Cut
  Tool = -> Cylinder002
FEATURE [Part::Cut] Cut093  label="BaseInf001"
  Base = -> Cut001
  Tool = -> Cylinder011
FEATURE [Part::Cut] Cut094  label="BaseInf002"
  Base = -> Cut093
  Tool = -> Box003
FEATURE [Part::Fillet] Fillet003
  Base = -> Cut118
  EdgeLinks = -> Cut118 [Edge23]
  Edges = 1 edges r=1: [Edge23]
FEATURE [Part::Fillet] Fillet004
  Base = -> Fillet003
  EdgeLinks = -> Fillet003 [Edge4]
  Edges = 1 edges r=1: [Edge4]
FEATURE [Part::Fillet] Fillet005  label="PortaSensor_Inclinacion001"
  Base = -> Fillet004
  EdgeLinks = -> Fillet004 [Edge34]
  Edges = 1 edges r=1: [Edge34]
  Placement = pos=(0,3.5,4) rot=(0,0,1;0rad)
FEATURE [Part::Fillet] Fillet006
  Base = -> Fillet005
  EdgeLinks = -> Fillet005 [Edge48]
  Edges = 1 edges r=1: [Edge48]
FEATURE [Part::Fillet] Fillet007  label="PortaSensor_TemHum"
  Base = -> Fillet006
  EdgeLinks = -> Fillet006 [Edge7,Edge18]
  Edges = 2 edges r=1: [Edge7,Edge18]
  Placement = pos=(-18,-9,137) rot=(0.57735,0.57735,-0.57735;2.0944rad)
FEATURE [Part::Fillet] Fillet009
  Base = -> Cylinder004
  EdgeLinks = -> Cylinder004 [Edge3]
  Edges = 1 edges r=1: [Edge3]
FEATURE [Part::Cut] Cut002
  Base = -> Fillet009
  Tool = -> Cylinder006
FEATURE [Part::Cut] Cut003
  Base = -> Cut002
  Placement = pos=(0,0,97) rot=(0,0,1;0rad)
  Tool = -> Cylinder005
FEATURE [Part::Fillet] Fillet010
  Base = -> Box001
  EdgeLinks = -> Box001 [Edge1,Edge3]
  Edges = 2 edges r=1.5: [Edge1,Edge3]
FEATURE [Part::Fillet] Fillet011  label="Lateral_Iz"
  Base = -> Fillet010
  EdgeLinks = -> Fillet010 [Edge17,Edge18]
  Edges = 2 edges r=1.5: [Edge17,Edge18]
FEATURE [Part::Fillet] Fillet012
  Base = -> Box002
  EdgeLinks = -> Box002 [Edge1,Edge3]
  Edges = 2 edges r=1.5: [Edge1,Edge3]
FEATURE [Part::Fillet] Fillet013  label="Lateral_De"
  Base = -> Fillet012
  EdgeLinks = -> Fillet012 [Edge17,Edge18]
  Edges = 2 edges r=1.5: [Edge17,Edge18]
  Placement = pos=(56,0,0) rot=(0,0,1;0rad)
FEATURE [Part::Fillet] Fillet019
  Base = -> Box006
  EdgeLinks = -> Box006 [Edge1,Edge3,Edge5,Edge7]
  Edges = 4 edges r=2: [Edge1,Edge3,Edge5,Edge7]
  Placement = pos=(-39,-4,0) rot=(0,0,1;0rad)
FEATURE [Part::Fillet] Fillet020
  Base = -> Box007
  EdgeLinks = -> Box007 [Edge1,Edge3,Edge5,Edge7]
  Edges = 4 edges r=2: [Edge1,Edge3,Edge5,Edge7]
  Placement = pos=(33,-4,0) rot=(0,0,1;0rad)
FEATURE [Part::Fillet] Fillet021
  Base = -> Box008
  EdgeLinks = -> Box008 [Edge1,Edge3,Edge5,Edge7]
  Edges = 4 edges r=2: [Edge1,Edge3,Edge5,Edge7]
  Placement = pos=(-39,-4,0) rot=(0,0,1;0rad)
FEATURE [Part::Cut] Cut095
  Base = -> Cut094
  Tool = -> Fillet021
FEATURE [Part::Cut] Cut096  label="BaseInf003"
  Base = -> Cut095
  Tool = -> Fillet020
FEATURE [Part::Fillet] Fillet022
  Base = -> Box009
  EdgeLinks = -> Box009 [Edge1,Edge3,Edge5,Edge7]
  Edges = 4 edges r=2: [Edge1,Edge3,Edge5,Edge7]
  Placement = pos=(33,-4,0) rot=(0,0,1;0rad)
FEATURE [Part::Fillet] Fillet032
  Base = -> Box095
  EdgeLinks = -> Box095 [Edge1,Edge3]
  Edges = 2 edges r=1.5: [Edge1,Edge3]
FEATURE [Part::Fillet] Fillet033  label="Lateral_De001"
  Base = -> Fillet032
  EdgeLinks = -> Fillet032 [Edge17,Edge18]
  Edges = 2 edges r=1.5: [Edge17,Edge18]
  Placement = pos=(56,0,0) rot=(0,0,1;0rad)
FEATURE [Part::Cut] Cut100
  Base = -> Fillet033
  Tool = -> Cylinder010
FEATURE [Part::Cut] Cut101
  Base = -> Cut100
  Tool = -> Cylinder009
FEATURE [Part::Cut] Cut102
  Base = -> Cut101
  Tool = -> Cylinder008
FEATURE [Part::Fillet] Fillet034
  Base = -> Box096
  EdgeLinks = -> Box096 [Edge1,Edge3]
  Edges = 2 edges r=1.5: [Edge1,Edge3]
FEATURE [Part::Fillet] Fillet035  label="Lateral_Iz001"
  Base = -> Fillet034
  EdgeLinks = -> Fillet034 [Edge17,Edge18]
  Edges = 2 edges r=1.5: [Edge17,Edge18]
FEATURE [Part::Cut] Cut097
  Base = -> Fillet035
  Tool = -> Cylinder071
FEATURE [Part::Cut] Cut098
  Base = -> Cut097
  Tool = -> Cylinder073
FEATURE [Part::Cut] Cut099  label="Lateral_Iz002"
  Base = -> Cut098
  Tool = -> Cylinder072
FEATURE [Part::Fillet] Fillet039
  Base = -> Box100
  EdgeLinks = -> Box100 [Edge7]
  Edges = 1 edges r=3: [Edge7]
FEATURE [Part::Cut] Cut112
  Base = -> Fillet039
  Tool = -> Cylinder085
FEATURE [Part::Fillet] Fillet040
  Base = -> Box101
  EdgeLinks = -> Box101 [Edge5]
  Edges = 1 edges r=3: [Edge5]
FEATURE [Part::Cut] Cut111
  Base = -> Fillet040
  Tool = -> Cylinder084
FEATURE [Part::Fillet] Fillet041
  Base = -> Cut111
  EdgeLinks = -> Cut111 [Edge15]
  Edges = 1 edges r=0.5: [Edge15]
  Placement = pos=(0,2,0) rot=(0,0,1;0rad)
FEATURE [Part::Fillet] Fillet042
  Base = -> Cut112
  EdgeLinks = -> Cut112 [Edge15]
  Edges = 1 edges r=0.5: [Edge15]
  Placement = pos=(0,2,0) rot=(0,0,1;0rad)
FEATURE [Part::Fillet] Fillet043
  Base = -> Cut116
  EdgeLinks = -> Cut116 [Edge23]
  Edges = 1 edges r=1: [Edge23]
FEATURE [Part::Fillet] Fillet001
  Base = -> Fillet043
  EdgeLinks = -> Fillet043 [Edge4]
  Edges = 1 edges r=1: [Edge4]
FEATURE [Part::Fillet] Fillet002  label="PortaSensor"
  Base = -> Fillet001
  EdgeLinks = -> Fillet001 [Edge34]
  Edges = 1 edges r=1: [Edge34]
  Placement = pos=(-12,11,110) rot=(0,0,1;0rad)
FEATURE [Part::Fillet] Fillet044
  Base = -> Fillet002
  EdgeLinks = -> Fillet002 [Edge48]
  Edges = 1 edges r=1: [Edge48]
FEATURE [Part::Fillet] Fillet045
  Base = -> Fillet044
  EdgeLinks = -> Fillet044 [Edge18]
  Edges = 1 edges r=1: [Edge18]
FEATURE [Part::Fillet] Fillet046
  Base = -> Fillet045
  EdgeLinks = -> Fillet045 [Edge22]
  Edges = 1 edges r=1: [Edge22]
FEATURE [Part::Fillet] Fillet049
  Base = -> Box110
  EdgeLinks = -> Box110 [Edge1,Edge3,Edge5,Edge7]
  Edges = 4 edges r=6: [Edge1,Edge3,Edge5,Edge7]
FEATURE [Part::Fillet] Fillet051
  Base = -> Box111
  EdgeLinks = -> Box111 [Edge1,Edge3]
  Edges = 2 edges r=1.5: [Edge1,Edge3]
FEATURE [Part::Fillet] Fillet052  label="Lateral_Iz006"
  Base = -> Fillet051
  EdgeLinks = -> Fillet051 [Edge17,Edge18]
  Edges = 2 edges r=1.5: [Edge17,Edge18]
FEATURE [Part::Cut] Cut120
  Base = -> Fillet052
  Tool = -> Cylinder086
FEATURE [Part::Cut] Cut121
  Base = -> Cut120
  Tool = -> Cylinder088
FEATURE [Part::Cut] Cut122  label="Lateral_Iz004"
  Base = -> Cut121
  Tool = -> Cylinder087
FEATURE [Part::Fillet] Fillet053
  Base = -> Box114
  EdgeLinks = -> Box114 [Edge1,Edge3]
  Edges = 2 edges r=1.5: [Edge1,Edge3]
FEATURE [Part::Fillet] Fillet054  label="Lateral_De005"
  Base = -> Fillet053
  EdgeLinks = -> Fillet053 [Edge17,Edge18]
  Edges = 2 edges r=1.5: [Edge17,Edge18]
  Placement = pos=(56,0,0) rot=(0,0,1;0rad)
FEATURE [Part::Cut] Cut124
  Base = -> Fillet054
  Tool = -> Cylinder091
FEATURE [Part::Cut] Cut125
  Base = -> Cut124
  Tool = -> Cylinder090
FEATURE [Part::Cut] Cut126
  Base = -> Cut125
  Tool = -> Cylinder089
FEATURE [Part::Fillet] Fillet058
  Base = -> Box118
  EdgeLinks = -> Box118 [Edge7]
  Edges = 1 edges r=3: [Edge7]
FEATURE [Part::Cut] Cut136
  Base = -> Fillet058
  Tool = -> Cylinder103
FEATURE [Part::Fillet] Fillet059
  Base = -> Box119
  EdgeLinks = -> Box119 [Edge5]
  Edges = 1 edges r=3: [Edge5]
FEATURE [Part::Cut] Cut135
  Base = -> Fillet059
  Tool = -> Cylinder102
FEATURE [Part::Fillet] Fillet060
  Base = -> Cut135
  EdgeLinks = -> Cut135 [Edge15]
  Edges = 1 edges r=0.5: [Edge15]
  Placement = pos=(0,2,0) rot=(0,0,1;0rad)
FEATURE [Part::Fillet] Fillet061
  Base = -> Cut136
  EdgeLinks = -> Cut136 [Edge15]
  Edges = 1 edges r=0.5: [Edge15]
  Placement = pos=(0,2,0) rot=(0,0,1;0rad)
FEATURE [Part::Fillet] Fillet062
  Base = -> Box120
  EdgeLinks = -> Box120 [Edge3,Edge7]
  Edges = 2 edges r=1.5: [Edge3,Edge7]
FEATURE [Part::Fillet] Fillet063
  Base = -> Fillet062
  EdgeLinks = -> Fillet062 [Edge2,Edge13]
  Edges = 2 edges r=1.5: [Edge2,Edge13]
  Placement = pos=(0,0,-3) rot=(0,0,1;0rad)
FEATURE [Part::Fillet] Fillet064
  Base = -> Box121
  EdgeLinks = -> Box121 [Edge3,Edge7]
  Edges = 2 edges r=1.5: [Edge3,Edge7]
FEATURE [Part::Fillet] Fillet065
  Base = -> Fillet064
  EdgeLinks = -> Fillet064 [Edge2,Edge13]
  Edges = 2 edges r=1.5: [Edge2,Edge13]
  Placement = pos=(0,0,-3) rot=(0,0,1;0rad)
FEATURE [Part::Fillet] Fillet069
  Base = -> Cut144
  EdgeLinks = -> Cut144 [Edge23]
  Edges = 1 edges r=1: [Edge23]
FEATURE [Part::Fillet] Fillet070
  Base = -> Fillet069
  EdgeLinks = -> Fillet069 [Edge4]
  Edges = 1 edges r=1: [Edge4]
FEATURE [Part::Fillet] Fillet071  label="PortaSensor_Inclinacion002"
  Base = -> Fillet070
  EdgeLinks = -> Fillet070 [Edge34]
  Edges = 1 edges r=1: [Edge34]
  Placement = pos=(0,3.5,4) rot=(0,0,1;0rad)
FEATURE [Part::Fillet] Fillet072
  Base = -> Fillet071
  EdgeLinks = -> Fillet071 [Edge48]
  Edges = 1 edges r=1: [Edge48]
FEATURE [Part::Fillet] Fillet073  label="PortaSensor_TemHum001"
  Base = -> Fillet072
  EdgeLinks = -> Fillet072 [Edge7,Edge18]
  Edges = 2 edges r=1: [Edge7,Edge18]
  Placement = pos=(17.5,13,140) rot=(0.57735,-0.57735,-0.57735;4.18879rad)
FEATURE [Part::Fillet] Fillet081
  Base = -> Cut150
  EdgeLinks = -> Cut150 [Edge23]
  Edges = 1 edges r=1: [Edge23]
FEATURE [Part::Fillet] Fillet082  label="PortaSensor_Inclinación"
  Base = -> Fillet081
  EdgeLinks = -> Fillet081 [Edge8]
  Edges = 1 edges r=1: [Edge8]
  Placement = pos=(-10,-11,110) rot=(1,0,0;1.5708rad)
FEATURE [Part::Fillet] Fillet083
  Base = -> Cut153
  EdgeLinks = -> Cut153 [Edge13,Edge29]
  Edges = 2 edges r=1.5: [Edge13,Edge29]
FEATURE [Part::Fillet] Fillet084  label="PortaPilas_9V"
  Base = -> Fillet083
  EdgeLinks = -> Fillet083 [Edge23,Edge41]
  Edges = 2 edges r=1.5: [Edge23,Edge41]
FEATURE [Part::Fillet] Fillet120
  Base = -> Cylinder134
  EdgeLinks = -> Cylinder134 [Edge3]
  Edges = 1 edges r=1: [Edge3]
FEATURE [Part::Cut] Cut205
  Base = -> Fillet120
  Tool = -> Cylinder136
FEATURE [Part::Cut] Cut206  label="BaseInf010"
  Base = -> Cut205
  Tool = -> Cylinder135
FEATURE [Part::Cut] Cut207  label="BaseInf011"
  Base = -> Cut206
  Tool = -> Cylinder137
FEATURE [Part::Cut] Cut208  label="BaseInf012"
  Base = -> Cut207
  Tool = -> Box170
FEATURE [Part::Fillet] Fillet121
  Base = -> Box171
  EdgeLinks = -> Box171 [Edge1,Edge3,Edge5,Edge7]
  Edges = 4 edges r=2: [Edge1,Edge3,Edge5,Edge7]
  Placement = pos=(33,-4,0) rot=(0,0,1;0rad)
FEATURE [Part::Fillet] Fillet122
  Base = -> Box172
  EdgeLinks = -> Box172 [Edge1,Edge3,Edge5,Edge7]
  Edges = 4 edges r=2: [Edge1,Edge3,Edge5,Edge7]
  Placement = pos=(-39,-4,0) rot=(0,0,1;0rad)
FEATURE [Part::Cut] Cut209
  Base = -> Cut208
  Tool = -> Fillet122
FEATURE [Part::Cut] Cut210  label="BaseInf013"
  Base = -> Cut209
  Tool = -> Fillet121
FEATURE [Part::Fillet] Fillet123
  Base = -> Box173
  EdgeLinks = -> Box173 [Edge1,Edge3]
  Edges = 2 edges r=1.5: [Edge1,Edge3]
FEATURE [Part::Fillet] Fillet124  label="Lateral_Iz010"
  Base = -> Fillet123
  EdgeLinks = -> Fillet123 [Edge17,Edge18]
  Edges = 2 edges r=1.5: [Edge17,Edge18]
FEATURE [Part::Cut] Cut211
  Base = -> Fillet124
  Tool = -> Cylinder138
FEATURE [Part::Cut] Cut212
  Base = -> Cut211
  Tool = -> Cylinder140
FEATURE [Part::Cut] Cut213  label="Lateral_Iz008"
  Base = -> Cut212
  Tool = -> Cylinder139
FEATURE [Part::Fillet] Fillet125
  Base = -> Box176
  EdgeLinks = -> Box176 [Edge1,Edge3]
  Edges = 2 edges r=1.5: [Edge1,Edge3]
FEATURE [Part::Fillet] Fillet126  label="Lateral_De009"
  Base = -> Fillet125
  EdgeLinks = -> Fillet125 [Edge17,Edge18]
  Edges = 2 edges r=1.5: [Edge17,Edge18]
  Placement = pos=(56,0,0) rot=(0,0,1;0rad)
FEATURE [Part::Cut] Cut215
  Base = -> Fillet126
  Tool = -> Cylinder143
FEATURE [Part::Cut] Cut216
  Base = -> Cut215
  Tool = -> Cylinder142
FEATURE [Part::Cut] Cut217
  Base = -> Cut216
  Tool = -> Cylinder141
FEATURE [Part::Fillet] Fillet130
  Base = -> Box180
  EdgeLinks = -> Box180 [Edge7]
  Edges = 1 edges r=3: [Edge7]
FEATURE [Part::Cut] Cut227
  Base = -> Fillet130
  Tool = -> Cylinder155
FEATURE [Part::Fillet] Fillet131
  Base = -> Box181
  EdgeLinks = -> Box181 [Edge5]
  Edges = 1 edges r=3: [Edge5]
FEATURE [Part::Cut] Cut226
  Base = -> Fillet131
  Tool = -> Cylinder154
FEATURE [Part::Fillet] Fillet132
  Base = -> Cut226
  EdgeLinks = -> Cut226 [Edge15]
  Edges = 1 edges r=0.5: [Edge15]
  Placement = pos=(0,2,0) rot=(0,0,1;0rad)
FEATURE [Part::Fillet] Fillet133
  Base = -> Cut227
  EdgeLinks = -> Cut227 [Edge15]
  Edges = 1 edges r=0.5: [Edge15]
  Placement = pos=(0,2,0) rot=(0,0,1;0rad)
FEATURE [Part::Fillet] Fillet134
  Base = -> Box182
  EdgeLinks = -> Box182 [Edge3,Edge7]
  Edges = 2 edges r=1.5: [Edge3,Edge7]
FEATURE [Part::Fillet] Fillet135
  Base = -> Fillet134
  EdgeLinks = -> Fillet134 [Edge2,Edge13]
  Edges = 2 edges r=1.5: [Edge2,Edge13]
  Placement = pos=(0,0,-3) rot=(0,0,1;0rad)
FEATURE [Part::Fillet] Fillet136
  Base = -> Box183
  EdgeLinks = -> Box183 [Edge3,Edge7]
  Edges = 2 edges r=1.5: [Edge3,Edge7]
FEATURE [Part::Fillet] Fillet137
  Base = -> Fillet136
  EdgeLinks = -> Fillet136 [Edge2,Edge13]
  Edges = 2 edges r=1.5: [Edge2,Edge13]
  Placement = pos=(0,0,-3) rot=(0,0,1;0rad)
FEATURE [Part::Fillet] Fillet145
  Base = -> Cylinder162
  EdgeLinks = -> Cylinder162 [Edge3]
  Edges = 1 edges r=0.5: [Edge3]
FEATURE [Part::Fillet] Fillet146
  Base = -> Fillet145
  EdgeLinks = -> Fillet145 [Edge3]
  Edges = 1 edges r=0.5: [Edge3]
FEATURE [Part::Fillet] Fillet147
  Base = -> Cylinder163
  EdgeLinks = -> Cylinder163 [Edge3]
  Edges = 1 edges r=0.5: [Edge3]
FEATURE [Part::Fillet] Fillet148
  Base = -> Fillet147
  EdgeLinks = -> Fillet147 [Edge3]
  Edges = 1 edges r=0.5: [Edge3]
FEATURE [Part::MultiFuse] Fusion069
  Shapes = -> [Cylinder074,Cylinder075]
FEATURE [Part::MultiFuse] Fusion070
  Shapes = -> [Box097,Fusion069]
FEATURE [Part::MultiFuse] Fusion071
  Shapes = -> [Fusion070,Box098]
FEATURE [Part::Cut] Cut103
  Base = -> Fusion071
  Tool = -> Cylinder076
FEATURE [Part::Cut] Cut104  label="Servo002"
  Base = -> Cut103
  Tool = -> Cylinder077
FEATURE [Part::MultiFuse] Fusion072
  Shapes = -> [Cylinder078,Box099]
FEATURE [Part::Fillet] Fillet036
  Base = -> Fusion072
  EdgeLinks = -> Fusion072 [Edge4]
  Edges = 1 edges r=2: [Edge4]
FEATURE [Part::Fillet] Fillet037
  Base = -> Fillet036
  EdgeLinks = -> Fillet036 [Edge25]
  Edges = 1 edges r=1: [Edge25]
FEATURE [Part::Fillet] Fillet038
  Base = -> Fillet037
  EdgeLinks = -> Fillet037 [Edge17]
  Edges = 1 edges r=1: [Edge17]
FEATURE [Part::MultiFuse] Fusion073
  Shapes = -> [Cut104,Fillet038]
FEATURE [Part::Cut] Cut105
  Base = -> Fusion073
  Tool = -> Cylinder079
FEATURE [Part::Cut] Cut106
  Base = -> Cut105
  Tool = -> Cylinder083
FEATURE [Part::Cut] Cut107
  Base = -> Cut106
  Tool = -> Cylinder082
FEATURE [Part::Cut] Cut108
  Base = -> Cut107
  Tool = -> Cylinder081
FEATURE [Part::Cut] Cut109  label="Servo003"
  Base = -> Cut108
  Placement = pos=(41,12,85) rot=(0.707107,-0.707107,0;3.14159rad)
  Tool = -> Cylinder080
FEATURE [Part::Cut] Cut110
  Base = -> Cut102
  Tool = -> Cut109
FEATURE [Part::MultiFuse] Fusion
  Shapes = -> [Cut110,Fillet041]
FEATURE [Part::MultiFuse] Fusion074  label="Lateral_De002"
  Shapes = -> [Fusion,Fillet042]
FEATURE [Part::MultiFuse] Fusion078
  Shapes = -> [Cylinder092,Cylinder093]
FEATURE [Part::MultiFuse] Fusion079
  Shapes = -> [Box115,Fusion078]
FEATURE [Part::MultiFuse] Fusion080
  Shapes = -> [Fusion079,Box116]
FEATURE [Part::Cut] Cut127
  Base = -> Fusion080
  Tool = -> Cylinder094
FEATURE [Part::Cut] Cut128  label="Servo004"
  Base = -> Cut127
  Tool = -> Cylinder095
FEATURE [Part::MultiFuse] Fusion081
  Shapes = -> [Cylinder096,Box117]
FEATURE [Part::Fillet] Fillet055
  Base = -> Fusion081
  EdgeLinks = -> Fusion081 [Edge4]
  Edges = 1 edges r=2: [Edge4]
FEATURE [Part::Fillet] Fillet056
  Base = -> Fillet055
  EdgeLinks = -> Fillet055 [Edge25]
  Edges = 1 edges r=1: [Edge25]
FEATURE [Part::Fillet] Fillet057
  Base = -> Fillet056
  EdgeLinks = -> Fillet056 [Edge17]
  Edges = 1 edges r=1: [Edge17]
FEATURE [Part::MultiFuse] Fusion082
  Shapes = -> [Cut128,Fillet057]
FEATURE [Part::Cut] Cut129
  Base = -> Fusion082
  Tool = -> Cylinder097
FEATURE [Part::Cut] Cut130
  Base = -> Cut129
  Tool = -> Cylinder101
FEATURE [Part::Cut] Cut131
  Base = -> Cut130
  Tool = -> Cylinder100
FEATURE [Part::Cut] Cut132
  Base = -> Cut131
  Tool = -> Cylinder099
FEATURE [Part::Cut] Cut133  label="Servo005"
  Base = -> Cut132
  Placement = pos=(41,12,85) rot=(0.707107,-0.707107,0;3.14159rad)
  Tool = -> Cylinder098
FEATURE [Part::Cut] Cut134
  Base = -> Cut126
  Tool = -> Cut133
FEATURE [Part::MultiFuse] Fusion077
  Shapes = -> [Cut134,Fillet060]
FEATURE [Part::MultiFuse] Fusion083  label="Lateral_De006"
  Shapes = -> [Fusion077,Fillet061]
FEATURE [Part::MultiFuse] Fusion084
  Shapes = -> [Fillet073,Box130]
FEATURE [Part::Fillet] Fillet077
  Base = -> Fusion084
  EdgeLinks = -> Fusion084 [Edge2,Edge16]
  Edges = 2 edges r=1: [Edge2,Edge16]
FEATURE [Part::Fillet] Fillet078  label="PortaSensor_TemHum002"
  Base = -> Fillet077
  EdgeLinks = -> Fillet077 [Edge20,Edge56]
  Edges = 2 edges r=1: [Edge20,Edge56]
FEATURE [Part::Fillet] Fillet079
  Base = -> Fillet078
  EdgeLinks = -> Fillet078 [Edge45]
  Edges = 1 edges r=1.5: [Edge45]
FEATURE [Part::Fillet] Fillet080  label="PortaSensor_TemHum003"
  Base = -> Fillet079
  EdgeLinks = -> Fillet079 [Edge39]
  Edges = 1 edges r=1.5: [Edge39]
  Placement = pos=(1,15.5,0) rot=(0,0,1;0rad)
FEATURE [Part::MultiFuse] Fusion097
  Shapes = -> [Cylinder144,Cylinder145]
FEATURE [Part::MultiFuse] Fusion098
  Shapes = -> [Box177,Fusion097]
FEATURE [Part::MultiFuse] Fusion099
  Shapes = -> [Fusion098,Box178]
FEATURE [Part::Cut] Cut218
  Base = -> Fusion099
  Tool = -> Cylinder146
FEATURE [Part::Cut] Cut219  label="Servo006"
  Base = -> Cut218
  Tool = -> Cylinder147
FEATURE [Part::MultiFuse] Fusion100
  Shapes = -> [Cylinder148,Box179]
FEATURE [Part::Fillet] Fillet127
  Base = -> Fusion100
  EdgeLinks = -> Fusion100 [Edge4]
  Edges = 1 edges r=2: [Edge4]
FEATURE [Part::Fillet] Fillet128
  Base = -> Fillet127
  EdgeLinks = -> Fillet127 [Edge25]
  Edges = 1 edges r=1: [Edge25]
FEATURE [Part::Fillet] Fillet129
  Base = -> Fillet128
  EdgeLinks = -> Fillet128 [Edge17]
  Edges = 1 edges r=1: [Edge17]
FEATURE [Part::MultiFuse] Fusion101
  Shapes = -> [Cut219,Fillet129]
FEATURE [Part::Cut] Cut220
  Base = -> Fusion101
  Tool = -> Cylinder149
FEATURE [Part::Cut] Cut221
  Base = -> Cut220
  Tool = -> Cylinder153
FEATURE [Part::Cut] Cut222
  Base = -> Cut221
  Tool = -> Cylinder152
FEATURE [Part::Cut] Cut223
  Base = -> Cut222
  Tool = -> Cylinder151
FEATURE [Part::Cut] Cut224  label="Servo007"
  Base = -> Cut223
  Placement = pos=(41,12,85) rot=(0.707107,-0.707107,0;3.14159rad)
  Tool = -> Cylinder150
FEATURE [Part::Cut] Cut225
  Base = -> Cut217
  Tool = -> Cut224
FEATURE [Part::MultiFuse] Fusion096
  Shapes = -> [Cut225,Fillet132]
FEATURE [Part::MultiFuse] Fusion102  label="Lateral_De010"
  Shapes = -> [Fusion096,Fillet133]
FEATURE [Part::Offset] Offset
  Fill = false
  Intersection = false
  Join = 0
  Mode = 0
  SelfIntersection = false
  Source = -> Fillet011
  Value = 0.2
FEATURE [Part::Cut] Cut004
  Base = -> Cut003
  Tool = -> Offset
FEATURE [Part::Offset] Offset001
  Fill = false
  Intersection = false
  Join = 0
  Mode = 0
  SelfIntersection = false
  Source = -> Fillet013
  Value = 0.2
FEATURE [Part::Cut] Cut005  label="Base_2"
  Base = -> Cut004
  Placement = pos=(0,0,10) rot=(0,0,1;0rad)
  Tool = -> Offset001
FEATURE [Part::Cut] Cut012
  Base = -> Cut005
  Tool = -> Fillet019
FEATURE [Part::Cut] Cut013
  Base = -> Cut012
  Tool = -> Fillet022
FEATURE [Part::MultiFuse] Fusion002  label="BaseSup"
  Shapes = -> [Cut013,Cut017]
FEATURE [Part::MultiFuse] Fusion075  label="BaseSup001"
  Shapes = -> [Fusion002,Fillet046]
FEATURE [Part::Fillet] Fillet047
  Base = -> Fusion075
  EdgeLinks = -> Fusion075 [Edge125]
  Edges = 1 edges r=2: [Edge125]
FEATURE [Part::Fillet] Fillet048
  Base = -> Fillet047
  EdgeLinks = -> Fillet047 [Edge136]
  Edges = 1 edges r=2: [Edge136]
FEATURE [Part::MultiFuse] Fusion076
  Shapes = -> [Fillet048,Fillet007]
FEATURE [Part::Chamfer] Chamfer  label="BaseSup002"
  Base = -> Fusion076
  EdgeLinks = -> Fusion076 [Edge137]
  Edges = 1 edges r=2: [Edge137]
FEATURE [Part::Cut] Cut119
  Base = -> Chamfer
  Tool = -> Fillet049
FEATURE [Part::Fillet] Fillet050  label="BaseSup003"
  Base = -> Cut119
  EdgeLinks = -> Cut119 [Edge41,Edge45]
  Edges = 2 edges r=1: [Edge41,Edge45]
FEATURE [Part::Cut] Cut147  label="BaseInf007"
  Base = -> Fillet050
  Tool = -> Box128
FEATURE [Part::Cut] Cut148
  Base = -> Cut147
  Tool = -> Box129
FEATURE [Part::Cut] Cut151  label="BaseSup004"
  Base = -> Cut148
  Tool = -> Box134
FEATURE [Part::MultiFuse] Fusion085
  Shapes = -> [Cut151,Fillet084]
FEATURE [Part::MultiFuse] Fusion086
  Shapes = -> [Fusion085,Fillet082]
FEATURE [Part::MultiFuse] Fusion087  label="BaseSup005"
  Shapes = -> [Fusion086,Fillet080]
FEATURE [Part::Cut] Cut235
  Base = -> Fusion087
  Tool = -> Box184
FEATURE [Part::Fillet] Fillet141
  Base = -> Cut235
  EdgeLinks = -> Cut235 [Edge15]
  Edges = 1 edges r=2.5: [Edge15]
FEATURE [Part::Fillet] Fillet142
  Base = -> Fillet141
  EdgeLinks = -> Fillet141 [Edge97]
  Edges = 1 edges r=2.5: [Edge97]
FEATURE [Part::Fillet] Fillet143
  Base = -> Fillet142
  EdgeLinks = -> Fillet142 [Edge20]
  Edges = 1 edges r=2.5: [Edge20]
FEATURE [Part::Fillet] Fillet144  label="BloquComponentes"
  Base = -> Fillet143
  EdgeLinks = -> Fillet143 [Edge92]
  Edges = 1 edges r=2.5: [Edge92]
FEATURE [Part::MultiFuse] Fusion103
  Shapes = -> [Fillet144,Cylinder158]
FEATURE [Part::MultiFuse] Fusion104
  Shapes = -> [Fusion103,Cylinder161]
FEATURE [Part::MultiFuse] Fusion105
  Shapes = -> [Fusion104,Cylinder160]
FEATURE [Part::MultiFuse] Fusion106
  Shapes = -> [Fusion105,Cylinder159]
FEATURE [Part::MultiFuse] Fusion107
  Shapes = -> [Fusion106,Fillet146]
FEATURE [Part::MultiFuse] Fusion108
  Shapes = -> [Fusion107,Fillet148]
FEATURE [Part::Offset] Offset002
  Fill = false
  Intersection = false
  Join = 0
  Mode = 0
  SelfIntersection = false
  Source = -> Box
  Value = 0.2
FEATURE [Part::Cut] Cut114  label="Lateral_De003"
  Base = -> Fusion074
  Tool = -> Offset002
FEATURE [Part::Cut] Cut177
  Base = -> Cut114
  Tool = -> Box165
FEATURE [Part::Cut] Cut179
  Base = -> Cut177
  Tool = -> Box167
FEATURE [Part::Cut] Cut181
  Base = -> Cut179
  Tool = -> Cylinder110
FEATURE [Part::Cut] Cut182
  Base = -> Cut181
  Tool = -> Cylinder111
FEATURE [Part::Cut] Cut183
  Base = -> Cut182
  Tool = -> Cylinder112
FEATURE [Part::Cut] Cut184
  Base = -> Cut183
  Tool = -> Cylinder120
FEATURE [Part::Cut] Cut185
  Base = -> Cut184
  Tool = -> Cylinder119
FEATURE [Part::Cut] Cut186
  Base = -> Cut185
  Tool = -> Cylinder118
FEATURE [Part::Cut] Cut187
  Base = -> Cut186
  Tool = -> Cylinder117
FEATURE [Part::Cut] Cut188
  Base = -> Cut187
  Tool = -> Cylinder116
FEATURE [Part::Cut] Cut189
  Base = -> Cut188
  Tool = -> Cylinder115
FEATURE [Part::Cut] Cut190
  Base = -> Cut189
  Tool = -> Cylinder114
FEATURE [Part::Cut] Cut191  label="LateralDer"
  Base = -> Cut190
  Tool = -> Cylinder113
FEATURE [Part::Cut] Cut202
  Base = -> Cut191
  Tool = -> Box168
FEATURE [Part::Cut] Cut203  label="LateralDer001"
  Base = -> Cut202
  Tool = -> Box169
FEATURE [Part::Cut] Cut255  label="LateralDer002"
  Base = -> Cut203
  Tool = -> Box197
FEATURE [Part::Cut] Cut256  label="LateralDer003"
  Base = -> Cut255
  Tool = -> Box198
FEATURE [Part::Offset] Offset003
  Fill = false
  Intersection = false
  Join = 0
  Mode = 0
  SelfIntersection = false
  Source = -> Box102
  Value = 0.2
FEATURE [Part::Cut] Cut113  label="Lateral_Iz003"
  Base = -> Cut099
  Tool = -> Offset003
FEATURE [Part::Cut] Cut178
  Base = -> Cut113
  Tool = -> Box166
FEATURE [Part::Cut] Cut180
  Base = -> Cut178
  Tool = -> Cylinder109
FEATURE [Part::Cut] Cut192
  Base = -> Cut180
  Tool = -> Cylinder121
FEATURE [Part::Cut] Cut193
  Base = -> Cut192
  Tool = -> Cylinder130
FEATURE [Part::Cut] Cut194
  Base = -> Cut193
  Tool = -> Cylinder129
FEATURE [Part::MultiFuse] Fusion095
  Shapes = -> [Cut194,Cylinder128]
FEATURE [Part::Cut] Cut195
  Base = -> Fusion095
  Tool = -> Cylinder127
FEATURE [Part::Cut] Cut196
  Base = -> Cut195
  Tool = -> Cylinder126
FEATURE [Part::Cut] Cut197
  Base = -> Cut196
  Tool = -> Cylinder125
FEATURE [Part::Cut] Cut198
  Base = -> Cut197
  Tool = -> Cylinder124
FEATURE [Part::Cut] Cut199
  Base = -> Cut198
  Tool = -> Cylinder123
FEATURE [Part::Cut] Cut200
  Base = -> Cut199
  Tool = -> Cylinder122
FEATURE [Part::Cut] Cut201  label="LateralIzq"
  Base = -> Cut200
  Tool = -> Cylinder131
FEATURE [Part::Offset] Offset004
  Fill = false
  Intersection = false
  Join = 0
  Mode = 0
  SelfIntersection = false
  Source = -> Box112
  Value = 0.2
FEATURE [Part::Cut] Cut123  label="Lateral_Iz005"
  Base = -> Cut122
  Tool = -> Offset004
FEATURE [Part::Cut] Cut138
  Base = -> Cut096
  Tool = -> Cut123
FEATURE [Part::Offset] Offset005
  Fill = false
  Intersection = false
  Join = 0
  Mode = 0
  SelfIntersection = false
  Source = -> Box113
  Value = 0.2
FEATURE [Part::Cut] Cut137  label="Lateral_De004"
  Base = -> Fusion083
  Tool = -> Offset005
FEATURE [Part::Cut] Cut139  label="BaseInf004"
  Base = -> Cut138
  Tool = -> Cut137
FEATURE [Part::Offset] Offset006
  Fill = false
  Intersection = false
  Join = 0
  Mode = 0
  SelfIntersection = false
  Source = -> Fillet063
  Value = 0.2
FEATURE [Part::Cut] Cut140
  Base = -> Cut139
  Tool = -> Offset006
FEATURE [Part::Offset] Offset007
  Fill = false
  Intersection = false
  Join = 0
  Mode = 0
  Placement = pos=(56,0,0) rot=(0,0,1;0rad)
  SelfIntersection = false
  Source = -> Fillet065
  Value = 0.2
FEATURE [Part::Cut] Cut141
  Base = -> Cut140
  Tool = -> Offset007
FEATURE [Part::Fillet] Fillet066
  Base = -> Cut141
  EdgeLinks = -> Cut141 [Edge55,Edge56,Edge57,Edge58,Edge59,Edge60,Edge61]
  Edges = 7 edges r=1: [Edge55,Edge56,Edge57,Edge58,Edge59,Edge60,Edge61]
FEATURE [Part::Fillet] Fillet067
  Base = -> Fillet066
  EdgeLinks = -> Fillet066 [Edge34,Edge38]
  Edges = 2 edges r=1: [Edge34,Edge38]
FEATURE [Part::Fillet] Fillet068  label="BaseInf005"
  Base = -> Fillet067
  EdgeLinks = -> Fillet067 [Edge28,Edge32]
  Edges = 2 edges r=1: [Edge28,Edge32]
FEATURE [Part::Cut] Cut142  label="BaseInf006"
  Base = -> Fillet068
  Tool = -> Cylinder104
FEATURE [Part::Cut] Cut204  label="BaseInf009"
  Base = -> Cut142
  Tool = -> Cylinder133
FEATURE [Part::Offset] Offset010
  Fill = false
  Intersection = false
  Join = 0
  Mode = 0
  SelfIntersection = false
  Source = -> Box174
  Value = 0.2
FEATURE [Part::Cut] Cut214  label="Lateral_Iz009"
  Base = -> Cut213
  Tool = -> Offset010
FEATURE [Part::Cut] Cut229
  Base = -> Cut210
  Tool = -> Cut214
FEATURE [Part::Offset] Offset011
  Fill = false
  Intersection = false
  Join = 0
  Mode = 0
  SelfIntersection = false
  Source = -> Box175
  Value = 0.2
FEATURE [Part::Cut] Cut228  label="Lateral_De008"
  Base = -> Fusion102
  Tool = -> Offset011
FEATURE [Part::Cut] Cut230  label="BaseInf014"
  Base = -> Cut229
  Tool = -> Cut228
FEATURE [Part::Offset] Offset012
  Fill = false
  Intersection = false
  Join = 0
  Mode = 0
  SelfIntersection = false
  Source = -> Fillet135
  Value = 0.2
FEATURE [Part::Cut] Cut231
  Base = -> Cut230
  Tool = -> Offset012
FEATURE [Part::Offset] Offset013
  Fill = false
  Intersection = false
  Join = 0
  Mode = 0
  Placement = pos=(56,0,0) rot=(0,0,1;0rad)
  SelfIntersection = false
  Source = -> Fillet137
  Value = 0.2
FEATURE [Part::Cut] Cut232
  Base = -> Cut231
  Tool = -> Offset013
FEATURE [Part::Fillet] Fillet138
  Base = -> Cut232
  EdgeLinks = -> Cut232 [Edge55,Edge56,Edge57,Edge58,Edge59,Edge60,Edge61]
  Edges = 7 edges r=1: [Edge55,Edge56,Edge57,Edge58,Edge59,Edge60,Edge61]
FEATURE [Part::Fillet] Fillet139
  Base = -> Fillet138
  EdgeLinks = -> Fillet138 [Edge34,Edge38]
  Edges = 2 edges r=1: [Edge34,Edge38]
FEATURE [Part::Fillet] Fillet140  label="BaseInf017"
  Base = -> Fillet139
  EdgeLinks = -> Fillet139 [Edge28,Edge32]
  Edges = 2 edges r=1: [Edge28,Edge32]
FEATURE [Part::Cut] Cut233  label="BaseInf015"
  Base = -> Fillet140
  Tool = -> Cylinder156
FEATURE [Part::Cut] Cut234  label="BaseSup012"
  Base = -> Cut233
  Placement = pos=(0,0,105) rot=(0,0,1;0rad)
  Tool = -> Cylinder157
FEATURE [Part::MultiFuse] Fusion109  label="BaseSup013"
  Shapes = -> [Cut234,Fusion108]
FEATURE [Part::MultiFuse] Fusion178  label="Capsula_Paracaidas"
  Shapes = -> [Cut201,Cut204,Fusion109,Cut256]
